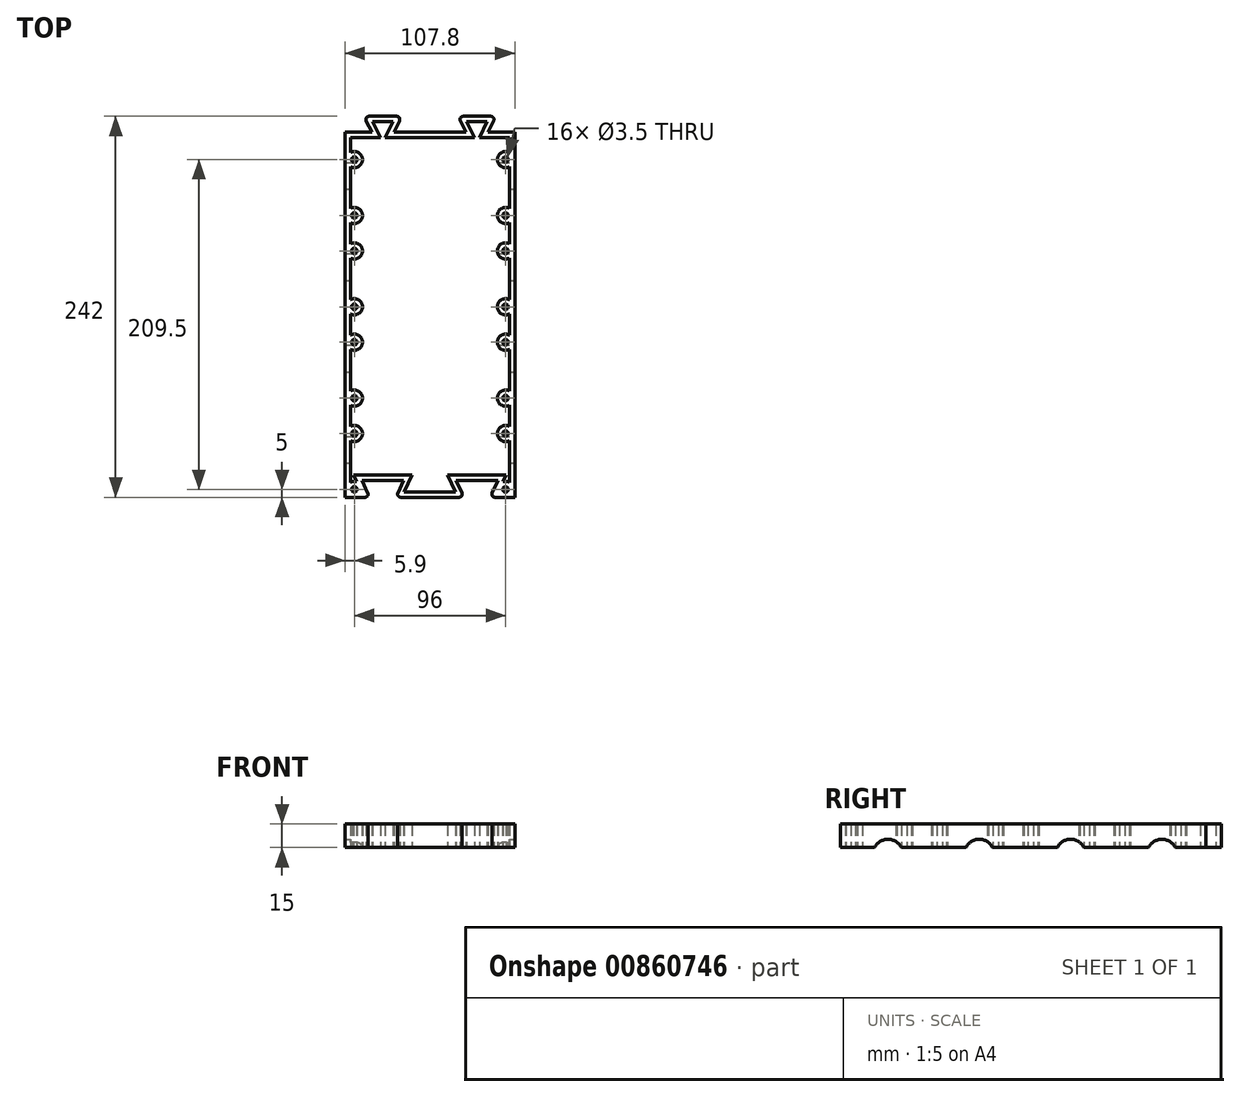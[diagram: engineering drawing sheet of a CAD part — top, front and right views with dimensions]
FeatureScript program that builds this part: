
annotation { "Feature Type Name" : "Feature", "Feature Type Description" : "" }
export const myFeature = defineFeature(function(context is Context, id is Id, definition is map)
    precondition{}
    {
        {
            var Q0;
            Q0=qCreatedBy(makeId("Top.planeOp"),FACE);
            var sketch = newSketch(context, id + "F0", { "sketchPlane" : qUnion([Q0])});
            skPoint(sketch, "E0", {"position": v(0, -232) * mm});
            skPoint(sketch, "E1", {"position": v(107.8, 0) * mm});
            skPoint(sketch, "E2", {"position": v(107.8, -232) * mm});
            skLineSegment(sketch, "E3", {"start": v(0, 0) * mm, "end": v(0, -232) * mm});
            skLineSegment(sketch, "E4", {"start": v(107.8, 0) * mm, "end": v(107.8, -232) * mm});
            skPoint(sketch, "E5", {"position": v(24, 0) * mm});
            skPoint(sketch, "E6", {"position": v(83.8, 0) * mm});
            skPoint(sketch, "E7", {"position": v(83.8, 10) * mm});
            skPoint(sketch, "E8", {"position": v(24, 10) * mm});
            skPoint(sketch, "E9", {"position": v(12, 10) * mm});
            skPoint(sketch, "E10", {"position": v(36, 10) * mm});
            skPoint(sketch, "E11", {"position": v(71.8, 10) * mm});
            skPoint(sketch, "E12", {"position": v(95.8, 10) * mm});
            skPoint(sketch, "E13", {"position": v(17, 0) * mm});
            skPoint(sketch, "E14", {"position": v(31, 0) * mm});
            skPoint(sketch, "E15", {"position": v(76.8, 0) * mm});
            skPoint(sketch, "E16", {"position": v(90.8, 0) * mm});
            skLineSegment(sketch, "E17", {"start": v(0, 0) * mm, "end": v(17, 0) * mm});
            skLineSegment(sketch, "E18", {"start": v(17, 0) * mm, "end": v(12, 10) * mm});
            skLineSegment(sketch, "E19", {"start": v(12, 10) * mm, "end": v(36, 10) * mm});
            skLineSegment(sketch, "E20", {"start": v(36, 10) * mm, "end": v(31, 0) * mm});
            skLineSegment(sketch, "E21", {"start": v(31, 0) * mm, "end": v(76.8, 0) * mm});
            skLineSegment(sketch, "E22", {"start": v(76.8, 0) * mm, "end": v(71.8, 10) * mm});
            skLineSegment(sketch, "E23", {"start": v(71.8, 10) * mm, "end": v(95.8, 10) * mm});
            skLineSegment(sketch, "E24", {"start": v(95.8, 10) * mm, "end": v(90.8, 0) * mm});
            skLineSegment(sketch, "E25", {"start": v(90.8, 0) * mm, "end": v(107.8, 0) * mm});
            skPoint(sketch, "E26", {"position": v(83.8, -232) * mm});
            skPoint(sketch, "E27", {"position": v(24, -232) * mm});
            skPoint(sketch, "E28", {"position": v(24, -221.25) * mm});
            skPoint(sketch, "E29", {"position": v(83.8, -221.25) * mm});
            skPoint(sketch, "E30", {"position": v(10.75, -221.25) * mm});
            skPoint(sketch, "E31", {"position": v(37.25, -221.25) * mm});
            skPoint(sketch, "E32", {"position": v(97.05, -221.25) * mm});
            skPoint(sketch, "E33", {"position": v(70.55, -221.25) * mm});
            skPoint(sketch, "E34", {"position": v(75.55, -232) * mm});
            skPoint(sketch, "E35", {"position": v(92.05, -232) * mm});
            skPoint(sketch, "E36", {"position": v(32.25, -232) * mm});
            skPoint(sketch, "E37", {"position": v(15.75, -232) * mm});
            skLineSegment(sketch, "E38", {"start": v(0, -232) * mm, "end": v(15.75, -232) * mm});
            skLineSegment(sketch, "E39", {"start": v(15.75, -232) * mm, "end": v(10.75, -221.25) * mm});
            skLineSegment(sketch, "E40", {"start": v(10.75, -221.25) * mm, "end": v(37.25, -221.25) * mm});
            skLineSegment(sketch, "E41", {"start": v(37.25, -221.25) * mm, "end": v(32.25, -232) * mm});
            skLineSegment(sketch, "E42", {"start": v(32.25, -232) * mm, "end": v(75.55, -232) * mm});
            skLineSegment(sketch, "E43", {"start": v(75.55, -232) * mm, "end": v(70.55, -221.25) * mm});
            skLineSegment(sketch, "E44", {"start": v(70.55, -221.25) * mm, "end": v(97.05, -221.25) * mm});
            skLineSegment(sketch, "E45", {"start": v(97.05, -221.25) * mm, "end": v(92.05, -232) * mm});
            skLineSegment(sketch, "E46", {"start": v(92.05, -232) * mm, "end": v(107.8, -232) * mm});
            skPoint(sketch, "E47", {"position": v(5.9, -227) * mm});
            skPoint(sketch, "E48", {"position": v(5.9, -191.5) * mm});
            skPoint(sketch, "E49.endSnap0", {"position": v(99.93, -232) * mm});
            skCircle(sketch, "E50", {"center": v(5.9, -227) * mm, "radius": 1.75 * mm});
            skCircle(sketch, "E51", {"center": v(5.9, -191.5) * mm, "radius": 1.75 * mm});
            skCircle(sketch, "E52.0.1.0", {"center": v(5.9, -169) * mm, "radius": 1.75 * mm});
            skCircle(sketch, "E52.0.2.0", {"center": v(5.9, -111) * mm, "radius": 1.75 * mm});
            skCircle(sketch, "E52.0.3.0", {"center": v(5.9, -53) * mm, "radius": 1.75 * mm});
            skCircle(sketch, "E52.1.0.0", {"center": v(101.9, -227) * mm, "radius": 1.75 * mm});
            skCircle(sketch, "E52.1.1.0", {"center": v(101.9, -169) * mm, "radius": 1.75 * mm});
            skCircle(sketch, "E52.1.2.0", {"center": v(101.9, -111) * mm, "radius": 1.75 * mm});
            skCircle(sketch, "E52.1.3.0", {"center": v(101.9, -53) * mm, "radius": 1.75 * mm});
            skLineSegment(sketch, "E52.direction1", {"start": v(5.9, -227) * mm, "end": v(101.9, -227) * mm, "construction": true});
            skLineSegment(sketch, "E52.direction2", {"start": v(5.9, -227) * mm, "end": v(5.9, -169) * mm, "construction": true});
            skLineSegment(sketch, "E53.direction2", {"start": v(5.9, -191.5) * mm, "end": v(5.9, -133.5) * mm, "construction": true});
            skCircle(sketch, "E54.0.1.0", {"center": v(5.9, -133.5) * mm, "radius": 1.75 * mm});
            skCircle(sketch, "E54.0.2.0", {"center": v(5.9, -75.5) * mm, "radius": 1.75 * mm});
            skCircle(sketch, "E54.0.3.0", {"center": v(5.9, -17.5) * mm, "radius": 1.75 * mm});
            skCircle(sketch, "E54.1.0.0", {"center": v(101.9, -191.5) * mm, "radius": 1.75 * mm});
            skCircle(sketch, "E54.1.1.0", {"center": v(101.9, -133.5) * mm, "radius": 1.75 * mm});
            skCircle(sketch, "E54.1.2.0", {"center": v(101.9, -75.5) * mm, "radius": 1.75 * mm});
            skCircle(sketch, "E54.1.3.0", {"center": v(101.9, -17.5) * mm, "radius": 1.75 * mm});
            skLineSegment(sketch, "E54.direction1", {"start": v(5.9, -191.5) * mm, "end": v(101.9, -191.5) * mm, "construction": true});
            skSolve(sketch);
        }
        {
            var Q0;
            Q0=makeQuery(id+"F0.imprint","IMPRINT",FACE,{"disambiguationData":[TD([[makeQuery(id+"F0.imprint","IMPRINT",EDGE,{"derivedFrom":sQuery(id+"F0.wireOp",EDGE,"E3")}),1.0]])]});
            var Q1;
            {var subQ3=sQuery(id+"F0.wireOp",EDGE,"E18");Q1=makeQuery(id+"F0.imprint","IMPRINT",FACE,{"disambiguationData":[TD([[makeQuery(id+"F0.imprint","IMPRINT",EDGE,{"derivedFrom":subQ3}),-1.0]])]});}
            var Q2;
            {var subQ0=sQuery(id+"F0.wireOp",EDGE,"E4");Q2=makeQuery(id+"F0.imprint","IMPRINT",FACE,{"disambiguationData":[TD([[makeQuery(id+"F0.imprint","IMPRINT",EDGE,{"derivedFrom":subQ0}),-1.0]])]});}
            extrude(context, id + "F1", {"entities" : qUnion([Q0, Q1, Q2]), "depth" : 15 * mm, "offsetDistance" : 25 * mm});
        }
        {
            var Q0;
            Q0=makeQuery(id+"F1.opExtrude","CAP_FACE",FACE,{"disambiguationData":[OSD([sQuery(id+"F0.wireOp",EDGE,"E3"),sQuery(id+"F0.wireOp",EDGE,"E4"),sQuery(id+"F0.wireOp",EDGE,"E17"),sQuery(id+"F0.wireOp",EDGE,"E18"),sQuery(id+"F0.wireOp",EDGE,"E19"),sQuery(id+"F0.wireOp",EDGE,"E20"),sQuery(id+"F0.wireOp",EDGE,"E21"),sQuery(id+"F0.wireOp",EDGE,"E22"),sQuery(id+"F0.wireOp",EDGE,"E23"),sQuery(id+"F0.wireOp",EDGE,"E24"),sQuery(id+"F0.wireOp",EDGE,"E25"),sQuery(id+"F0.wireOp",EDGE,"E38"),sQuery(id+"F0.wireOp",EDGE,"E39"),sQuery(id+"F0.wireOp",EDGE,"E40"),sQuery(id+"F0.wireOp",EDGE,"E41"),sQuery(id+"F0.wireOp",EDGE,"E42"),sQuery(id+"F0.wireOp",EDGE,"E43"),sQuery(id+"F0.wireOp",EDGE,"E44"),sQuery(id+"F0.wireOp",EDGE,"E45"),sQuery(id+"F0.wireOp",EDGE,"E46"),sQuery(id+"F0.wireOp",EDGE,"E50"),sQuery(id+"F0.wireOp",EDGE,"E51"),sQuery(id+"F0.wireOp",EDGE,"f23a599c-0a4c-42d7-8352-668d931a5bbb.0.1.0"),sQuery(id+"F0.wireOp",EDGE,"f23a599c-0a4c-42d7-8352-668d931a5bbb.0.2.0"),sQuery(id+"F0.wireOp",EDGE,"f23a599c-0a4c-42d7-8352-668d931a5bbb.0.3.0"),sQuery(id+"F0.wireOp",EDGE,"f23a599c-0a4c-42d7-8352-668d931a5bbb.1.0.0"),sQuery(id+"F0.wireOp",EDGE,"f23a599c-0a4c-42d7-8352-668d931a5bbb.1.1.0"),sQuery(id+"F0.wireOp",EDGE,"f23a599c-0a4c-42d7-8352-668d931a5bbb.1.2.0"),sQuery(id+"F0.wireOp",EDGE,"f23a599c-0a4c-42d7-8352-668d931a5bbb.1.3.0"),sQuery(id+"F0.wireOp",EDGE,"8d7e1e17-68d3-4274-bf32-06b6ae57f314.0.1.0"),sQuery(id+"F0.wireOp",EDGE,"8d7e1e17-68d3-4274-bf32-06b6ae57f314.0.2.0"),sQuery(id+"F0.wireOp",EDGE,"8d7e1e17-68d3-4274-bf32-06b6ae57f314.0.3.0"),sQuery(id+"F0.wireOp",EDGE,"8d7e1e17-68d3-4274-bf32-06b6ae57f314.1.0.0"),sQuery(id+"F0.wireOp",EDGE,"8d7e1e17-68d3-4274-bf32-06b6ae57f314.1.1.0"),sQuery(id+"F0.wireOp",EDGE,"8d7e1e17-68d3-4274-bf32-06b6ae57f314.1.2.0"),sQuery(id+"F0.wireOp",EDGE,"8d7e1e17-68d3-4274-bf32-06b6ae57f314.1.3.0")])],"isStart":false});
            var Q1;
            Q1=makeQuery(id+"F1.opExtrude","CAP_FACE",FACE,{"disambiguationData":[OSD([sQuery(id+"F0.wireOp",EDGE,"E3"),sQuery(id+"F0.wireOp",EDGE,"E4"),sQuery(id+"F0.wireOp",EDGE,"E17"),sQuery(id+"F0.wireOp",EDGE,"E18"),sQuery(id+"F0.wireOp",EDGE,"E19"),sQuery(id+"F0.wireOp",EDGE,"E20"),sQuery(id+"F0.wireOp",EDGE,"E21"),sQuery(id+"F0.wireOp",EDGE,"E22"),sQuery(id+"F0.wireOp",EDGE,"E23"),sQuery(id+"F0.wireOp",EDGE,"E24"),sQuery(id+"F0.wireOp",EDGE,"E25"),sQuery(id+"F0.wireOp",EDGE,"E38"),sQuery(id+"F0.wireOp",EDGE,"E39"),sQuery(id+"F0.wireOp",EDGE,"E40"),sQuery(id+"F0.wireOp",EDGE,"E41"),sQuery(id+"F0.wireOp",EDGE,"E42"),sQuery(id+"F0.wireOp",EDGE,"E43"),sQuery(id+"F0.wireOp",EDGE,"E44"),sQuery(id+"F0.wireOp",EDGE,"E45"),sQuery(id+"F0.wireOp",EDGE,"E46"),sQuery(id+"F0.wireOp",EDGE,"E50"),sQuery(id+"F0.wireOp",EDGE,"E51"),sQuery(id+"F0.wireOp",EDGE,"f23a599c-0a4c-42d7-8352-668d931a5bbb.0.1.0"),sQuery(id+"F0.wireOp",EDGE,"f23a599c-0a4c-42d7-8352-668d931a5bbb.0.2.0"),sQuery(id+"F0.wireOp",EDGE,"f23a599c-0a4c-42d7-8352-668d931a5bbb.0.3.0"),sQuery(id+"F0.wireOp",EDGE,"f23a599c-0a4c-42d7-8352-668d931a5bbb.1.0.0"),sQuery(id+"F0.wireOp",EDGE,"f23a599c-0a4c-42d7-8352-668d931a5bbb.1.1.0"),sQuery(id+"F0.wireOp",EDGE,"f23a599c-0a4c-42d7-8352-668d931a5bbb.1.2.0"),sQuery(id+"F0.wireOp",EDGE,"f23a599c-0a4c-42d7-8352-668d931a5bbb.1.3.0"),sQuery(id+"F0.wireOp",EDGE,"8d7e1e17-68d3-4274-bf32-06b6ae57f314.0.1.0"),sQuery(id+"F0.wireOp",EDGE,"8d7e1e17-68d3-4274-bf32-06b6ae57f314.0.2.0"),sQuery(id+"F0.wireOp",EDGE,"8d7e1e17-68d3-4274-bf32-06b6ae57f314.0.3.0"),sQuery(id+"F0.wireOp",EDGE,"8d7e1e17-68d3-4274-bf32-06b6ae57f314.1.0.0"),sQuery(id+"F0.wireOp",EDGE,"8d7e1e17-68d3-4274-bf32-06b6ae57f314.1.1.0"),sQuery(id+"F0.wireOp",EDGE,"8d7e1e17-68d3-4274-bf32-06b6ae57f314.1.2.0"),sQuery(id+"F0.wireOp",EDGE,"8d7e1e17-68d3-4274-bf32-06b6ae57f314.1.3.0")])],"isStart":true});
            shell(context, id + "F2", {"entities" : qUnion([Q0, Q1]), "thickness" : 3.4 * mm});
        }
        {
            var Q0;
            Q0=makeQuery(id+"F1.opExtrude","SWEPT_EDGE",EDGE,{"disambiguationData":[OSD([sQuery(id+"F0.wireOp",EDGE,"E38"),sQuery(id+"F0.wireOp",EDGE,"E39")])]});
            var Q1;
            Q1=makeQuery(id+"F1.opExtrude","SWEPT_EDGE",EDGE,{"disambiguationData":[OSD([sQuery(id+"F0.wireOp",EDGE,"E41"),sQuery(id+"F0.wireOp",EDGE,"E42")])]});
            var Q2;
            Q2=makeQuery(id+"F1.opExtrude","SWEPT_EDGE",EDGE,{"disambiguationData":[OSD([sQuery(id+"F0.wireOp",EDGE,"E42"),sQuery(id+"F0.wireOp",EDGE,"E43")])]});
            var Q3;
            Q3=makeQuery(id+"F1.opExtrude","SWEPT_EDGE",EDGE,{"disambiguationData":[OSD([sQuery(id+"F0.wireOp",EDGE,"E45"),sQuery(id+"F0.wireOp",EDGE,"E46")])]});
            var Q4;
            Q4=makeQuery(id+"F1.opExtrude","SWEPT_EDGE",EDGE,{"disambiguationData":[OSD([sQuery(id+"F0.wireOp",EDGE,"E18"),sQuery(id+"F0.wireOp",EDGE,"E19")])]});
            var Q5;
            Q5=makeQuery(id+"F1.opExtrude","SWEPT_EDGE",EDGE,{"disambiguationData":[OSD([sQuery(id+"F0.wireOp",EDGE,"E19"),sQuery(id+"F0.wireOp",EDGE,"E20")])]});
            var Q6;
            Q6=makeQuery(id+"F1.opExtrude","SWEPT_EDGE",EDGE,{"disambiguationData":[OSD([sQuery(id+"F0.wireOp",EDGE,"E22"),sQuery(id+"F0.wireOp",EDGE,"E23")])]});
            var Q7;
            Q7=makeQuery(id+"F1.opExtrude","SWEPT_EDGE",EDGE,{"disambiguationData":[OSD([sQuery(id+"F0.wireOp",EDGE,"E23"),sQuery(id+"F0.wireOp",EDGE,"E24")])]});
            fillet(context, id + "F3", {"entities" : qUnion([Q0, Q1, Q2, Q3, Q4, Q5, Q6, Q7]), "radius" : 2 * mm, "tangentPropagation" : true, "allowEdgeOverflow" : false});
        }
        {
            var Q0;
            Q0=makeQuery(id+"F1.opExtrude","SWEPT_FACE",FACE,{"disambiguationData":[OSD([sQuery(id+"F0.wireOp",EDGE,"E4")])]});
            var sketch = newSketch(context, id + "F4", { "sketchPlane" : qUnion([Q0])});
            skArc(sketch, "E55", {"start": v(-193.3, 0) * mm, "mid": v(-201.79, 5.28) * mm, "end": v(-210.27, 0) * mm});
            skArc(sketch, "E56.1.0.0", {"start": v(-135.3, 0) * mm, "mid": v(-143.79, 5.28) * mm, "end": v(-152.27, 0) * mm});
            skArc(sketch, "E56.2.0.0", {"start": v(-77.3, 0) * mm, "mid": v(-85.79, 5.28) * mm, "end": v(-94.27, 0) * mm});
            skArc(sketch, "E56.3.0.0", {"start": v(-19.3, 0) * mm, "mid": v(-27.79, 5.28) * mm, "end": v(-36.27, 0) * mm});
            skLineSegment(sketch, "E56.direction1", {"start": v(-210.27, 0) * mm, "end": v(-152.27, 0) * mm, "construction": true});
            skSolve(sketch);
        }
        {
            var Q0;
            {var subQ0=sQuery(id+"F4.wireOp",EDGE,"E55");Q0=makeQuery(id+"F4.imprint","IMPRINT",FACE,{"disambiguationData":[TD([[makeQuery(id+"F4.imprint","IMPRINT",EDGE,{"derivedFrom":subQ0}),1.0]])]});}
            var Q1;
            {var subQ0=sQuery(id+"F4.wireOp",EDGE,"E56.1.0.0");Q1=makeQuery(id+"F4.imprint","IMPRINT",FACE,{"disambiguationData":[TD([[makeQuery(id+"F4.imprint","IMPRINT",EDGE,{"derivedFrom":subQ0}),1.0]])]});}
            var Q2;
            {var subQ0=sQuery(id+"F4.wireOp",EDGE,"E56.2.0.0");Q2=makeQuery(id+"F4.imprint","IMPRINT",FACE,{"disambiguationData":[TD([[makeQuery(id+"F4.imprint","IMPRINT",EDGE,{"derivedFrom":subQ0}),1.0]])]});}
            var Q3;
            {var subQ0=sQuery(id+"F4.wireOp",EDGE,"E56.3.0.0");Q3=makeQuery(id+"F4.imprint","IMPRINT",FACE,{"disambiguationData":[TD([[makeQuery(id+"F4.imprint","IMPRINT",EDGE,{"derivedFrom":subQ0}),1.0]])]});}
            extrude(context, id + "F5", {"entities" : qUnion([Q0, Q1, Q2, Q3]), "operationType" : NewBodyOperationType.REMOVE, "oppositeDirection" : true, "depth" : 200 * mm, "offsetDistance" : 25 * mm});
        }
    });
